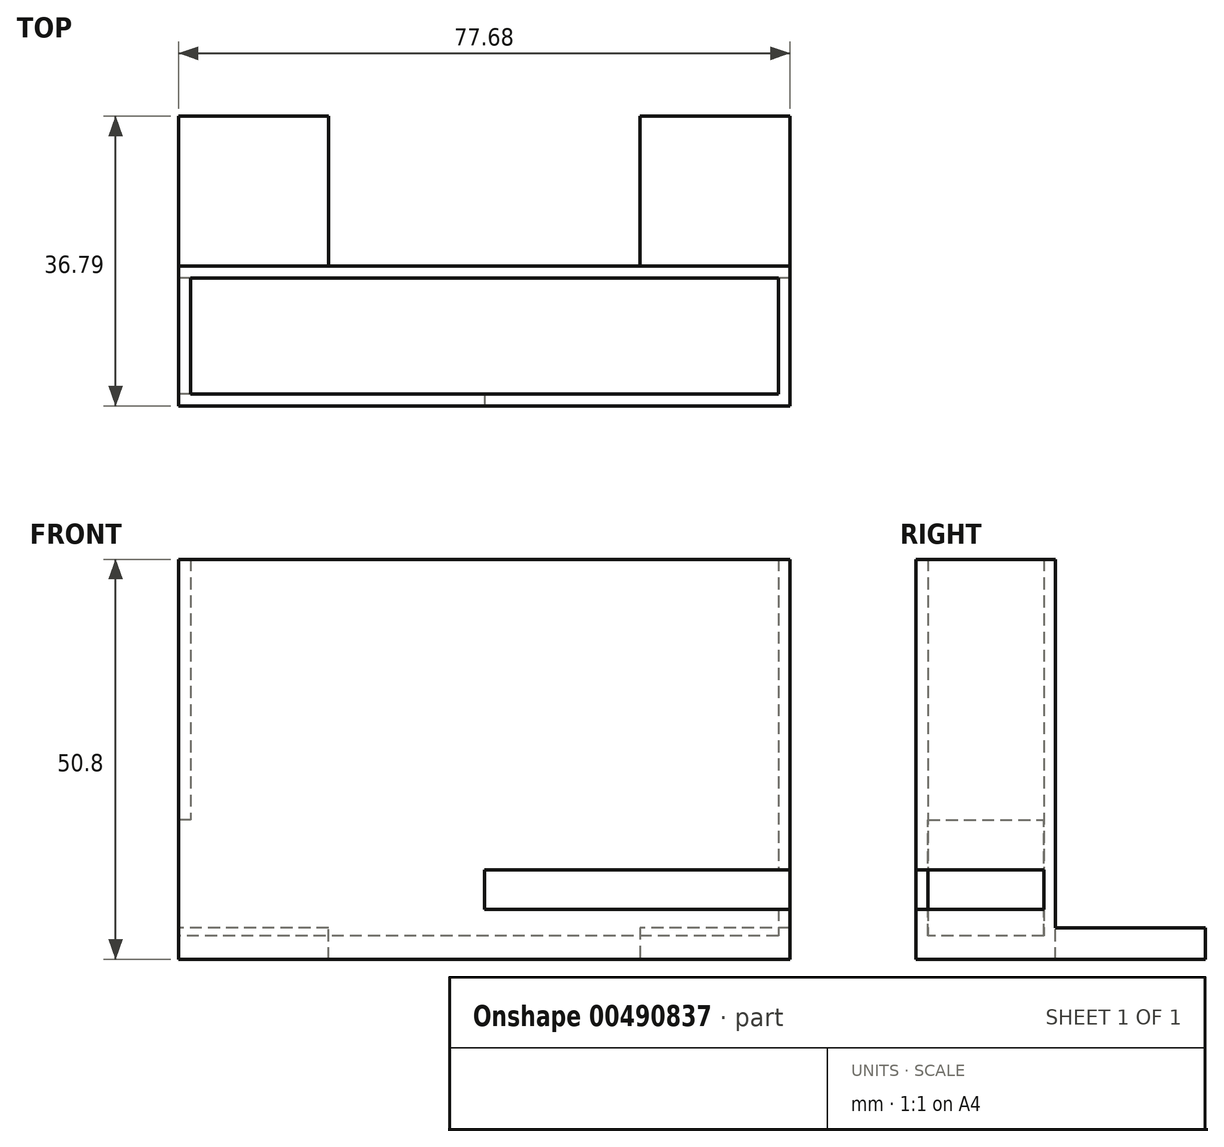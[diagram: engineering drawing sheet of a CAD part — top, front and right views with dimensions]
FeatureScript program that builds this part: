
annotation { "Feature Type Name" : "Feature", "Feature Type Description" : "" }
export const myFeature = defineFeature(function(context is Context, id is Id, definition is map)
    precondition{}
    {
        {
            var Q0;
            Q0=qCreatedBy(makeId("Top.planeOp"),FACE);
            var sketch = newSketch(context, id + "F0", { "sketchPlane" : qUnion([Q0])});
            skPoint(sketch, "E0.middle", {"position": v(0, 0) * mm});
            skLineSegment(sketch, "E1.bottom", {"start": v(38.84, -8.87) * mm, "end": v(-38.84, -8.87) * mm});
            skLineSegment(sketch, "E1.top", {"start": v(38.84, 8.87) * mm, "end": v(-38.84, 8.87) * mm});
            skLineSegment(sketch, "E1.left", {"start": v(38.84, -8.87) * mm, "end": v(38.84, 8.87) * mm});
            skLineSegment(sketch, "E1.right", {"start": v(-38.84, -8.87) * mm, "end": v(-38.84, 8.87) * mm});
            skLineSegment(sketch, "E2.bottom", {"start": v(37.34, 7.37) * mm, "end": v(-37.34, 7.37) * mm});
            skLineSegment(sketch, "E2.top", {"start": v(37.34, -7.37) * mm, "end": v(-37.34, -7.37) * mm});
            skLineSegment(sketch, "E2.left", {"start": v(37.34, 7.37) * mm, "end": v(37.34, -7.37) * mm});
            skLineSegment(sketch, "E2.right", {"start": v(-37.34, 7.37) * mm, "end": v(-37.34, -7.37) * mm});
            skSolve(sketch);
        }
        {
            var Q0;
            Q0=makeQuery(id+"F0.imprint","IMPRINT",FACE,{"disambiguationData":[TD([[makeQuery(id+"F0.imprint","IMPRINT",EDGE,{"derivedFrom":sQuery(id+"F0.wireOp",EDGE,"E1.bottom")}),-1.0]])]});
            extrude(context, id + "F1", {"entities" : qUnion([Q0]), "depth" : 50.8 * mm, "offsetDistance" : 25 * mm});
        }
        {
            var Q0;
            Q0=makeQuery(id+"F0.imprint","IMPRINT",FACE,{"disambiguationData":[TD([[makeQuery(id+"F0.imprint","IMPRINT",EDGE,{"derivedFrom":sQuery(id+"F0.wireOp",EDGE,"E2.bottom")}),1.0]])]});
            extrude(context, id + "F2", {"entities" : qUnion([Q0]), "operationType" : NewBodyOperationType.ADD, "depth" : 3 * mm, "offsetDistance" : 25 * mm});
        }
        {
            var Q0;
            Q0=makeQuery(id+"F1.opExtrude","SWEPT_FACE",FACE,{"disambiguationData":[OSD([sQuery(id+"F0.wireOp",EDGE,"E1.top")])]});
            var sketch = newSketch(context, id + "F3", { "sketchPlane" : qUnion([Q0])});
            skLineSegment(sketch, "E3", {"start": v(-38.84, 4) * mm, "end": v(-19.79, 4) * mm});
            skLineSegment(sketch, "E4", {"start": v(-19.79, 4) * mm, "end": v(-19.79, 0) * mm});
            skLineSegment(sketch, "E5", {"start": v(19.79, 0) * mm, "end": v(19.79, 4) * mm});
            skLineSegment(sketch, "E6", {"start": v(19.79, 4) * mm, "end": v(38.84, 4) * mm});
            skSolve(sketch);
        }
        {
            var Q0;
            {var subQ0=sQuery(id+"F3.wireOp",EDGE,"E3");Q0=makeQuery(id+"F3.imprint","IMPRINT",FACE,{"disambiguationData":[TD([[makeQuery(id+"F3.imprint","IMPRINT",EDGE,{"derivedFrom":subQ0}),-1.0]])]});}
            var Q1;
            {var subQ0=sQuery(id+"F3.wireOp",EDGE,"E5");Q1=makeQuery(id+"F3.imprint","IMPRINT",FACE,{"disambiguationData":[TD([[makeQuery(id+"F3.imprint","IMPRINT",EDGE,{"derivedFrom":subQ0}),-1.0]])]});}
            extrude(context, id + "F4", {"entities" : qUnion([Q0, Q1]), "operationType" : NewBodyOperationType.ADD, "depth" : 19.05 * mm, "offsetDistance" : 25 * mm});
        }
        {
            var Q0;
            {var subQ0=sQuery(id+"F0.wireOp",EDGE,"E1.right");Q0=makeQuery(id+"F4.boolean.opBoolean","MERGE",FACE,{"derivedFrom":[makeQuery(id+"F1.opExtrude","SWEPT_FACE",FACE,{"disambiguationData":[OSD([subQ0])]}),makeQuery(id+"F4.opExtrude","SWEPT_FACE",FACE,{"disambiguationData":[OSD([sQuery(id+"F0.wireOp",EDGE,"E1.top"),subQ0])]})]});}
            var sketch = newSketch(context, id + "F5", { "sketchPlane" : qUnion([Q0])});
            skLineSegment(sketch, "E7.bottom", {"start": v(-7.37, 3) * mm, "end": v(7.37, 3) * mm});
            skLineSegment(sketch, "E7.top", {"start": v(-7.37, 17.73) * mm, "end": v(7.37, 17.73) * mm});
            skLineSegment(sketch, "E7.left", {"start": v(-7.37, 3) * mm, "end": v(-7.37, 17.73) * mm});
            skLineSegment(sketch, "E7.right", {"start": v(7.37, 3) * mm, "end": v(7.37, 17.73) * mm});
            skSolve(sketch);
        }
        {
            var Q0;
            Q0=makeQuery(id+"F5.imprint","IMPRINT",FACE,{"disambiguationData":[TD([[makeQuery(id+"F5.imprint","IMPRINT",EDGE,{"derivedFrom":sQuery(id+"F5.wireOp",EDGE,"E7.bottom")}),1.0]])]});
            extrude(context, id + "F6", {"entities" : qUnion([Q0]), "operationType" : NewBodyOperationType.REMOVE, "oppositeDirection" : true, "depth" : 5 * mm, "offsetDistance" : 25 * mm});
        }
        {
            var Q0;
            Q0=makeQuery(id+"F1.opExtrude","SWEPT_FACE",FACE,{"disambiguationData":[OSD([sQuery(id+"F0.wireOp",EDGE,"E1.bottom")])]});
            var sketch = newSketch(context, id + "F7", { "sketchPlane" : qUnion([Q0])});
            skLineSegment(sketch, "E8.bottom", {"start": v(38.84, 6.35) * mm, "end": v(0, 6.35) * mm});
            skLineSegment(sketch, "E8.top", {"start": v(38.84, 11.35) * mm, "end": v(0, 11.35) * mm});
            skLineSegment(sketch, "E8.left", {"start": v(38.84, 6.35) * mm, "end": v(38.84, 11.35) * mm});
            skLineSegment(sketch, "E8.right", {"start": v(0, 6.35) * mm, "end": v(0, 11.35) * mm});
            skSolve(sketch);
        }
        {
            var Q0;
            Q0=makeQuery(id+"F7.imprint","IMPRINT",FACE,{"disambiguationData":[TD([[makeQuery(id+"F7.imprint","IMPRINT",EDGE,{"derivedFrom":sQuery(id+"F7.wireOp",EDGE,"E8.bottom")}),-1.0]])]});
            extrude(context, id + "F8", {"entities" : qUnion([Q0]), "operationType" : NewBodyOperationType.REMOVE, "oppositeDirection" : true, "depth" : 16.23 * mm, "offsetDistance" : 25 * mm});
        }
    });
